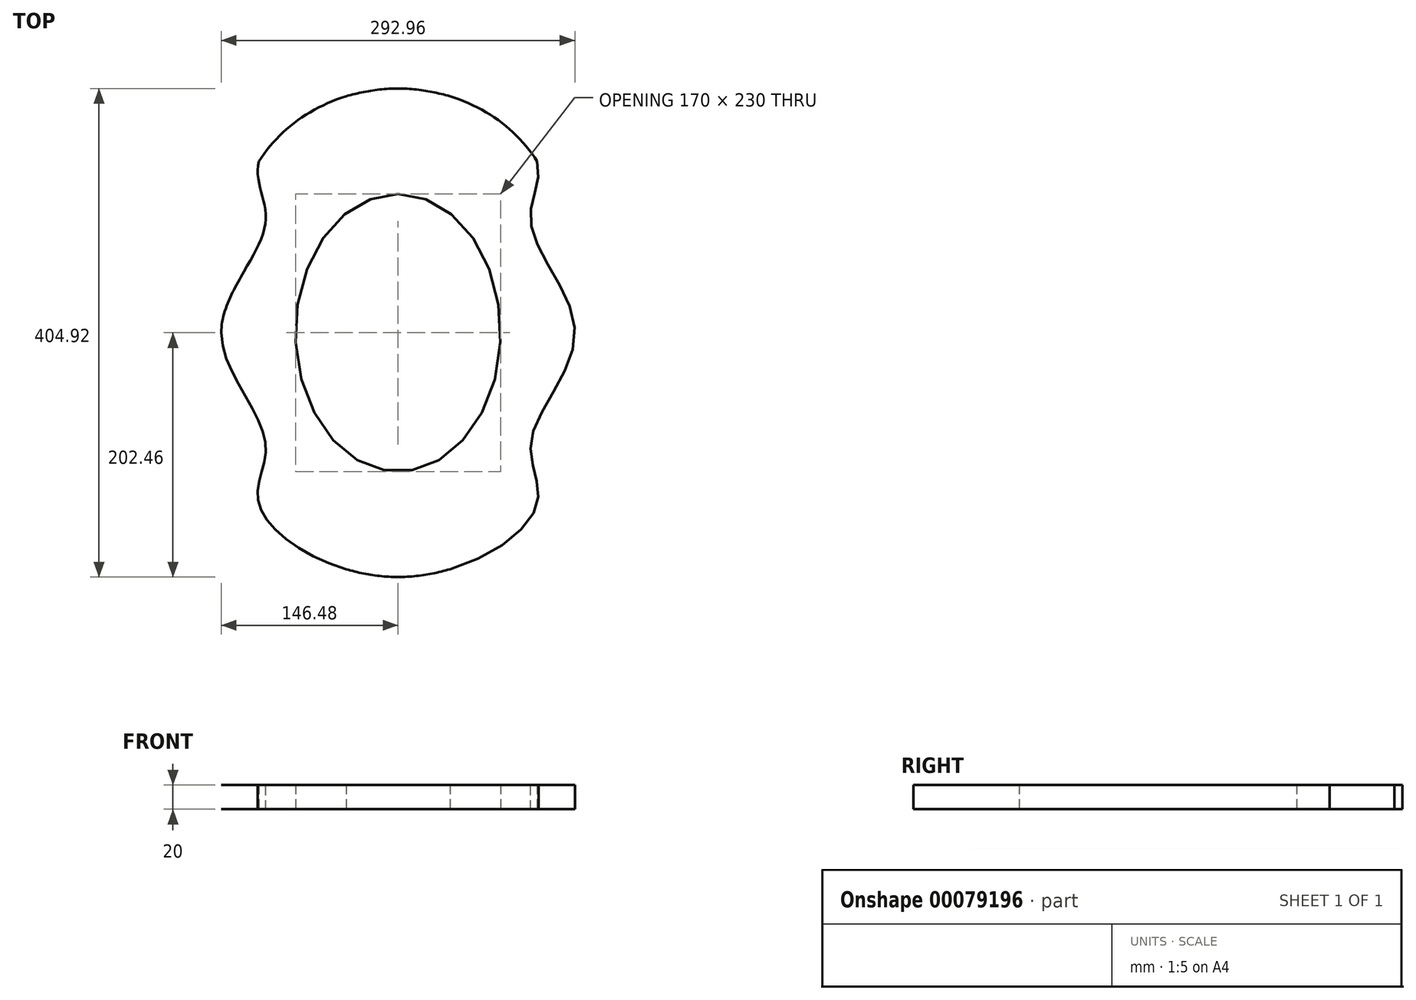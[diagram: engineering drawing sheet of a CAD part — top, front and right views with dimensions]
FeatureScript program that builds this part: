
annotation { "Feature Type Name" : "Feature", "Feature Type Description" : "" }
export const myFeature = defineFeature(function(context is Context, id is Id, definition is map)
    precondition{}
    {
        {
            var Q0;
            Q0=qCreatedBy(makeId("Top.planeOp"),FACE);
            var sketch = newSketch(context, id + "F0", { "sketchPlane" : qUnion([Q0])});
            skPoint(sketch, "E0", {"position": v(150.32, -165.76) * mm});
            skPoint(sketch, "E1", {"position": v(107.37, -221.56) * mm});
            skPoint(sketch, "E2", {"position": v(69.02, -211.72) * mm});
            skPoint(sketch, "E3", {"position": v(0, -246.18) * mm});
            skPoint(sketch, "E4", {"position": v(138.05, -177.25) * mm});
            skPoint(sketch, "E5", {"position": v(146.48, 0) * mm});
            skPoint(sketch, "E6", {"position": v(132.68, -82.88) * mm});
            skLineSegment(sketch, "E7", {"start": v(0, 292) * mm, "end": v(0, -246.18) * mm, "construction": true});
            skPoint(sketch, "E8.MirrorP", {"position": v(-146.48, 0) * mm});
            skPoint(sketch, "E9.MirrorP", {"position": v(-132.68, -82.88) * mm});
            skPoint(sketch, "E10.MirrorP", {"position": v(-150.32, -165.76) * mm});
            skPoint(sketch, "E11.MirrorP", {"position": v(-138.05, -177.25) * mm});
            skPoint(sketch, "E12.MirrorP", {"position": v(-107.37, -221.56) * mm});
            skPoint(sketch, "E13.MirrorP", {"position": v(-69.02, -211.72) * mm});
            skPoint(sketch, "E14", {"position": v(0, 0) * mm});
            skPoint(sketch, "E15", {"position": v(-146.25, -161.4) * mm});
            skPoint(sketch, "E16", {"position": v(-136.87, -189.28) * mm});
            skPoint(sketch, "E17", {"position": v(-146.26, -172.33) * mm});
            skPoint(sketch, "E18", {"position": v(-131.04, -210.06) * mm});
            skPoint(sketch, "E19", {"position": v(-94.82, -218.38) * mm});
            skPoint(sketch, "E20", {"position": v(-60.59, -222.84) * mm});
            skPoint(sketch, "E21", {"position": v(-67.25, -214.49) * mm});
            skPoint(sketch, "E22", {"position": v(-72.48, -210.2) * mm});
            skPoint(sketch, "E23", {"position": v(-119.37, -219.05) * mm});
            skPoint(sketch, "E24", {"position": v(-149.89, -167.68) * mm});
            skPoint(sketch, "E25.MirrorP", {"position": v(60.59, -222.84) * mm});
            skPoint(sketch, "E26.MirrorP", {"position": v(67.25, -214.49) * mm});
            skPoint(sketch, "E27.MirrorP", {"position": v(72.48, -210.2) * mm});
            skPoint(sketch, "E28.MirrorP", {"position": v(94.82, -218.38) * mm});
            skPoint(sketch, "E29.MirrorP", {"position": v(119.37, -219.05) * mm});
            skPoint(sketch, "E30.MirrorP", {"position": v(136.87, -189.28) * mm});
            skPoint(sketch, "E31.MirrorP", {"position": v(146.26, -172.33) * mm});
            skPoint(sketch, "E32.MirrorP", {"position": v(149.89, -167.68) * mm});
            skPoint(sketch, "E33.MirrorP", {"position": v(146.25, -161.4) * mm});
            skPoint(sketch, "E34", {"position": v(-139.73, -175.31) * mm});
            skPoint(sketch, "E35.MirrorP", {"position": v(131.04, -210.06) * mm});
            skPoint(sketch, "E36.MirrorP", {"position": v(-132.68, 82.88) * mm});
            skPoint(sketch, "E37.MirrorP", {"position": v(-139.73, 175.31) * mm});
            skPoint(sketch, "E38.MirrorP", {"position": v(-150.32, 165.76) * mm});
            skPoint(sketch, "E39.MirrorP", {"position": v(69.02, 211.72) * mm});
            skPoint(sketch, "E40.MirrorP", {"position": v(150.32, 165.76) * mm});
            skPoint(sketch, "E41.MirrorP", {"position": v(-67.25, 214.49) * mm});
            skPoint(sketch, "E42.MirrorP", {"position": v(131.04, 210.06) * mm});
            skPoint(sketch, "E43.MirrorP", {"position": v(60.59, 222.84) * mm});
            skPoint(sketch, "E44.MirrorP", {"position": v(119.37, 219.05) * mm});
            skPoint(sketch, "E45.MirrorP", {"position": v(136.87, 189.28) * mm});
            skPoint(sketch, "E46.MirrorP", {"position": v(-72.48, 210.2) * mm});
            skPoint(sketch, "E47.MirrorP", {"position": v(-138.05, 177.25) * mm});
            skPoint(sketch, "E48.MirrorP", {"position": v(-69.02, 211.72) * mm});
            skPoint(sketch, "E49.MirrorP", {"position": v(72.48, 210.2) * mm});
            skPoint(sketch, "E50.MirrorP", {"position": v(-146.25, 161.4) * mm});
            skPoint(sketch, "E51.MirrorP", {"position": v(-136.87, 189.28) * mm});
            skPoint(sketch, "E52.MirrorP", {"position": v(138.05, 177.25) * mm});
            skPoint(sketch, "E53.MirrorP", {"position": v(67.25, 214.49) * mm});
            skPoint(sketch, "E54.MirrorP", {"position": v(-149.89, 167.68) * mm});
            skPoint(sketch, "E55.MirrorP", {"position": v(149.89, 167.68) * mm});
            skPoint(sketch, "E56.MirrorP", {"position": v(-107.37, 221.56) * mm});
            skPoint(sketch, "E57.MirrorP", {"position": v(-94.82, 218.38) * mm});
            skPoint(sketch, "E58.MirrorP", {"position": v(146.26, 172.33) * mm});
            skPoint(sketch, "E59.MirrorP", {"position": v(107.37, 221.56) * mm});
            skPoint(sketch, "E60.MirrorP", {"position": v(-131.04, 210.06) * mm});
            skPoint(sketch, "E61.MirrorP", {"position": v(94.82, 218.38) * mm});
            skPoint(sketch, "E62.MirrorP", {"position": v(146.25, 161.4) * mm});
            skPoint(sketch, "E63.MirrorP", {"position": v(0, 246.18) * mm});
            skPoint(sketch, "E64.MirrorP", {"position": v(-146.26, 172.33) * mm});
            skPoint(sketch, "E65.MirrorP", {"position": v(-119.37, 219.05) * mm});
            skPoint(sketch, "E66.MirrorP", {"position": v(-60.59, 222.84) * mm});
            skPoint(sketch, "E67.MirrorP", {"position": v(132.68, 82.88) * mm});
            skFitSpline(sketch, "E68", {"points": [v(-146.48, 0) * mm, v(-132.68, 82.88) * mm, v(-146.25, 161.4) * mm, v(-150.32, 165.76) * mm, v(-149.89, 167.68) * mm, v(-146.26, 172.33) * mm, v(-139.73, 175.31) * mm, v(-138.05, 177.25) * mm, v(-136.87, 189.28) * mm, v(-131.04, 210.06) * mm, v(-119.37, 219.05) * mm, v(-107.37, 221.56) * mm, v(-94.82, 218.38) * mm, v(-72.48, 210.2) * mm, v(-69.02, 211.72) * mm, v(-67.25, 214.49) * mm, v(-60.59, 222.84) * mm, v(0, 246.18) * mm, v(60.59, 222.84) * mm, v(67.25, 214.49) * mm, v(69.02, 211.72) * mm, v(72.48, 210.2) * mm, v(94.82, 218.38) * mm, v(107.37, 221.56) * mm, v(119.37, 219.05) * mm, v(131.04, 210.06) * mm, v(136.87, 189.28) * mm, v(138.05, 177.25) * mm, v(146.26, 172.33) * mm, v(149.89, 167.68) * mm, v(150.32, 165.76) * mm, v(146.25, 161.4) * mm, v(132.68, 82.88) * mm, v(146.48, 0) * mm, v(132.68, -82.88) * mm, v(146.25, -161.4) * mm, v(150.32, -165.76) * mm, v(149.89, -167.68) * mm, v(146.26, -172.33) * mm, v(138.05, -177.25) * mm, v(136.87, -189.28) * mm, v(131.04, -210.06) * mm, v(119.37, -219.05) * mm, v(107.37, -221.56) * mm, v(94.82, -218.38) * mm, v(72.48, -210.2) * mm, v(69.02, -211.72) * mm, v(67.25, -214.49) * mm, v(60.59, -222.84) * mm, v(0, -246.18) * mm, v(-60.59, -222.84) * mm, v(-67.25, -214.49) * mm, v(-69.02, -211.72) * mm, v(-72.48, -210.2) * mm, v(-94.82, -218.38) * mm, v(-107.37, -221.56) * mm, v(-119.37, -219.05) * mm, v(-131.04, -210.06) * mm, v(-136.87, -189.28) * mm, v(-138.05, -177.25) * mm, v(-139.73, -175.31) * mm, v(-146.26, -172.33) * mm, v(-149.89, -167.68) * mm, v(-150.32, -165.76) * mm, v(-146.25, -161.4) * mm, v(-132.68, -82.88) * mm, v(-146.48, 0) * mm]});
            skPoint(sketch, "E69", {"position": v(0, 295) * mm});
            skPoint(sketch, "E70", {"position": v(-30, 295) * mm});
            skPoint(sketch, "E71", {"position": v(-225, 0) * mm});
            skPoint(sketch, "E72", {"position": v(-225, 100) * mm});
            skPoint(sketch, "E73.MirrorP", {"position": v(225, 100) * mm});
            skPoint(sketch, "E74.MirrorP", {"position": v(225, -60) * mm});
            skLineSegment(sketch, "E75", {"start": v(0, 0) * mm, "end": v(-373.3, 215.53) * mm, "construction": true});
            skLineSegment(sketch, "E76", {"start": v(0, 0) * mm, "end": v(-204.64, 354.44) * mm, "construction": true});
            skLineSegment(sketch, "E77", {"start": v(-225, 0) * mm, "end": v(-225, 100) * mm});
            skLineSegment(sketch, "E78", {"start": v(-30, 295) * mm, "end": v(0, 295) * mm});
            skPoint(sketch, "E79", {"position": v(-30, 100) * mm});
            skArc(sketch, "E80", {"start": v(-30, 295) * mm, "mid": v(-167.89, 237.89) * mm, "end": v(-225, 100) * mm});
            skLineSegment(sketch, "E81.MirrorCS", {"start": v(225, 0) * mm, "end": v(225, 100) * mm});
            skArc(sketch, "E82.MirrorCS", {"start": v(30, 295) * mm, "mid": v(167.89, 237.89) * mm, "end": v(225, 100) * mm});
            skLineSegment(sketch, "E83.MirrorCS", {"start": v(30, 295) * mm, "end": v(0, 295) * mm});
            skArc(sketch, "E84.MirrorCS", {"start": v(-30, -295) * mm, "mid": v(-167.89, -237.89) * mm, "end": v(-225, -100) * mm});
            skLineSegment(sketch, "E85.MirrorCS", {"start": v(-225, 0) * mm, "end": v(-225, -100) * mm});
            skLineSegment(sketch, "E86.MirrorCS", {"start": v(225, 0) * mm, "end": v(225, -100) * mm});
            skArc(sketch, "E87.MirrorCS", {"start": v(30, -295) * mm, "mid": v(167.89, -237.89) * mm, "end": v(225, -100) * mm});
            skLineSegment(sketch, "E88.MirrorCS", {"start": v(30, -295) * mm, "end": v(0, -295) * mm});
            skLineSegment(sketch, "E89.MirrorCS", {"start": v(-30, -295) * mm, "end": v(0, -295) * mm});
            skEllipse(sketch, "E90", {"center": v(0, 82.88) * mm, "majorRadius": 132.68 * mm, "minorRadius": 119.58 * mm, "majorAxis": v(1, 0)});
            skSolve(sketch);
        }
        {
            var Q0;
            {var subQ0=sQuery(id+"F0.wireOp",EDGE,"E90");var subQ1=sQuery(id+"F0.wireOp",EDGE,"E68");var subQ2=makeQuery(id+"F0.imprint","INTERSECT",VERTEX,{"disambiguationData":[OD(0.0)],"derivedFrom":[subQ1,subQ0]});Q0=makeQuery(id+"F0.imprint","IMPRINT",FACE,{"disambiguationData":[TD([[makeQuery(id+"F0.imprint","IMPRINT",EDGE,{"disambiguationData":[TD([[subQ2,1.0]])],"derivedFrom":subQ1}),-1.0]])]});}
            var sketch = newSketch(context, id + "F1", { "sketchPlane" : qUnion([Q0])});
            skFitSpline(sketch, "E91.0", {"points": [v(-146.48, 0) * mm, v(-146.48, 25.45) * mm, v(-122.55, 75.68) * mm, v(-141.58, 161.6) * mm, v(-150.97, 165.24) * mm, v(-149.84, 167.93) * mm, v(-146.88, 173.13) * mm, v(-139.54, 174.98) * mm, v(-137.39, 177.3) * mm, v(-137.38, 190.15) * mm, v(-133.28, 211.38) * mm, v(-119.9, 219.69) * mm, v(-106.83, 222.51) * mm, v(-95.46, 219.19) * mm, v(-72.9, 208.32) * mm, v(-68.89, 211.56) * mm, v(-66.98, 214.97) * mm, v(-60.9, 225.94) * mm, v(0, 260.58) * mm, v(60.9, 225.94) * mm, v(66.98, 214.97) * mm, v(68.89, 211.56) * mm, v(72.9, 208.32) * mm, v(95.47, 219.19) * mm, v(106.82, 222.52) * mm, v(119.95, 219.67) * mm, v(133.09, 211.44) * mm, v(138.2, 189.9) * mm, v(135.3, 175.97) * mm, v(146.9, 173.38) * mm, v(149.81, 167.94) * mm, v(150.98, 165.24) * mm, v(141.57, 161.6) * mm, v(122.55, 75.68) * mm, v(158.6, 0) * mm, v(122.55, -75.68) * mm, v(141.57, -161.6) * mm, v(150.98, -165.24) * mm, v(149.81, -167.94) * mm, v(146.9, -173.38) * mm, v(135.3, -175.97) * mm, v(138.2, -189.9) * mm, v(133.09, -211.44) * mm, v(119.95, -219.67) * mm, v(106.82, -222.52) * mm, v(95.47, -219.19) * mm, v(72.9, -208.32) * mm, v(68.89, -211.56) * mm, v(66.98, -214.97) * mm, v(60.9, -225.94) * mm, v(0, -260.58) * mm, v(-60.9, -225.94) * mm, v(-66.98, -214.97) * mm, v(-68.89, -211.56) * mm, v(-72.9, -208.32) * mm, v(-95.46, -219.19) * mm, v(-106.83, -222.51) * mm, v(-119.9, -219.69) * mm, v(-133.28, -211.38) * mm, v(-137.38, -190.15) * mm, v(-137.39, -177.3) * mm, v(-139.54, -174.98) * mm, v(-146.88, -173.13) * mm, v(-149.84, -167.93) * mm, v(-150.97, -165.24) * mm, v(-141.58, -161.6) * mm, v(-122.55, -75.68) * mm, v(-146.48, -25.45) * mm, v(-146.48, 0) * mm]});
            skEllipticalArc(sketch, "E92.0", {});
            skEllipticalArc(sketch, "E93.MirrorC", {});
            skFitSpline(sketch, "E94.trimOffspring", {"points": [v(-146.48, 0) * mm, v(-146.48, 25.45) * mm, v(-122.55, 75.68) * mm, v(-141.58, 161.6) * mm, v(-150.97, 165.24) * mm, v(-149.84, 167.93) * mm, v(-146.88, 173.13) * mm, v(-139.54, 174.98) * mm, v(-137.39, 177.3) * mm, v(-137.38, 190.15) * mm, v(-133.28, 211.38) * mm, v(-119.9, 219.69) * mm, v(-106.83, 222.51) * mm, v(-95.46, 219.19) * mm, v(-72.9, 208.32) * mm, v(-68.89, 211.56) * mm, v(-66.98, 214.97) * mm, v(-60.9, 225.94) * mm, v(0, 260.58) * mm, v(60.9, 225.94) * mm, v(66.98, 214.97) * mm, v(68.89, 211.56) * mm, v(72.9, 208.32) * mm, v(95.47, 219.19) * mm, v(106.82, 222.52) * mm, v(119.95, 219.67) * mm, v(133.09, 211.44) * mm, v(138.2, 189.9) * mm, v(135.3, 175.97) * mm, v(146.9, 173.38) * mm, v(149.81, 167.94) * mm, v(150.98, 165.24) * mm, v(141.57, 161.6) * mm, v(122.55, 75.68) * mm, v(158.6, 0) * mm, v(122.55, -75.68) * mm, v(141.57, -161.6) * mm, v(150.98, -165.24) * mm, v(149.81, -167.94) * mm, v(146.9, -173.38) * mm, v(135.3, -175.97) * mm, v(138.2, -189.9) * mm, v(133.09, -211.44) * mm, v(119.95, -219.67) * mm, v(106.82, -222.52) * mm, v(95.47, -219.19) * mm, v(72.9, -208.32) * mm, v(68.89, -211.56) * mm, v(66.98, -214.97) * mm, v(60.9, -225.94) * mm, v(0, -260.58) * mm, v(-60.9, -225.94) * mm, v(-66.98, -214.97) * mm, v(-68.89, -211.56) * mm, v(-72.9, -208.32) * mm, v(-95.46, -219.19) * mm, v(-106.83, -222.51) * mm, v(-119.9, -219.69) * mm, v(-133.28, -211.38) * mm, v(-137.38, -190.15) * mm, v(-137.39, -177.3) * mm, v(-139.54, -174.98) * mm, v(-146.88, -173.13) * mm, v(-149.84, -167.93) * mm, v(-150.97, -165.24) * mm, v(-141.58, -161.6) * mm, v(-122.55, -75.68) * mm, v(-146.48, -25.45) * mm, v(-146.48, 0) * mm]});
            skPoint(sketch, "E95", {"position": v(0, 202.46) * mm});
            skPoint(sketch, "E96", {"position": v(-110, 90) * mm});
            skPoint(sketch, "E97", {"position": v(-115, 143) * mm});
            skPoint(sketch, "E98.MirrorP", {"position": v(115, 143) * mm});
            skPoint(sketch, "E99.MirrorP", {"position": v(110, 90) * mm});
            skPoint(sketch, "E100.MirrorP", {"position": v(-110, -90) * mm});
            skPoint(sketch, "E101.MirrorP", {"position": v(-115, -143) * mm});
            skPoint(sketch, "E102.MirrorP", {"position": v(0, -202.46) * mm});
            skPoint(sketch, "E103.MirrorP", {"position": v(115, -143) * mm});
            skPoint(sketch, "E104.MirrorP", {"position": v(110, -90) * mm});
            skFitSpline(sketch, "E105", {"points": [v(-146.48, 0) * mm, v(-110, 90) * mm, v(-115, 143) * mm, v(0, 202.46) * mm, v(115, 143) * mm, v(110, 90) * mm, v(146.48, 0) * mm, v(110, -90) * mm, v(115, -143) * mm, v(0, -202.46) * mm, v(-115, -143) * mm, v(-110, -90) * mm, v(-146.48, 0) * mm]});
            skFitSpline(sketch, "E106.trimOffspring", {"points": [v(-146.48, 0) * mm, v(-146.48, 25.45) * mm, v(-122.55, 75.68) * mm, v(-141.58, 161.6) * mm, v(-150.97, 165.24) * mm, v(-149.84, 167.93) * mm, v(-146.88, 173.13) * mm, v(-139.54, 174.98) * mm, v(-137.39, 177.3) * mm, v(-137.38, 190.15) * mm, v(-133.28, 211.38) * mm, v(-119.9, 219.69) * mm, v(-106.83, 222.51) * mm, v(-95.46, 219.19) * mm, v(-72.9, 208.32) * mm, v(-68.89, 211.56) * mm, v(-66.98, 214.97) * mm, v(-60.9, 225.94) * mm, v(0, 260.58) * mm, v(60.9, 225.94) * mm, v(66.98, 214.97) * mm, v(68.89, 211.56) * mm, v(72.9, 208.32) * mm, v(95.47, 219.19) * mm, v(106.82, 222.52) * mm, v(119.95, 219.67) * mm, v(133.09, 211.44) * mm, v(138.2, 189.9) * mm, v(135.3, 175.97) * mm, v(146.9, 173.38) * mm, v(149.81, 167.94) * mm, v(150.98, 165.24) * mm, v(141.57, 161.6) * mm, v(122.55, 75.68) * mm, v(158.6, 0) * mm, v(122.55, -75.68) * mm, v(141.57, -161.6) * mm, v(150.98, -165.24) * mm, v(149.81, -167.94) * mm, v(146.9, -173.38) * mm, v(135.3, -175.97) * mm, v(138.2, -189.9) * mm, v(133.09, -211.44) * mm, v(119.95, -219.67) * mm, v(106.82, -222.52) * mm, v(95.47, -219.19) * mm, v(72.9, -208.32) * mm, v(68.89, -211.56) * mm, v(66.98, -214.97) * mm, v(60.9, -225.94) * mm, v(0, -260.58) * mm, v(-60.9, -225.94) * mm, v(-66.98, -214.97) * mm, v(-68.89, -211.56) * mm, v(-72.9, -208.32) * mm, v(-95.46, -219.19) * mm, v(-106.83, -222.51) * mm, v(-119.9, -219.69) * mm, v(-133.28, -211.38) * mm, v(-137.38, -190.15) * mm, v(-137.39, -177.3) * mm, v(-139.54, -174.98) * mm, v(-146.88, -173.13) * mm, v(-149.84, -167.93) * mm, v(-150.97, -165.24) * mm, v(-141.58, -161.6) * mm, v(-122.55, -75.68) * mm, v(-146.48, -25.45) * mm, v(-146.48, 0) * mm]});
            skFitSpline(sketch, "E107.trimOffspring", {"points": [v(-146.48, 0) * mm, v(-146.48, 25.45) * mm, v(-122.55, 75.68) * mm, v(-141.58, 161.6) * mm, v(-150.97, 165.24) * mm, v(-149.84, 167.93) * mm, v(-146.88, 173.13) * mm, v(-139.54, 174.98) * mm, v(-137.39, 177.3) * mm, v(-137.38, 190.15) * mm, v(-133.28, 211.38) * mm, v(-119.9, 219.69) * mm, v(-106.83, 222.51) * mm, v(-95.46, 219.19) * mm, v(-72.9, 208.32) * mm, v(-68.89, 211.56) * mm, v(-66.98, 214.97) * mm, v(-60.9, 225.94) * mm, v(0, 260.58) * mm, v(60.9, 225.94) * mm, v(66.98, 214.97) * mm, v(68.89, 211.56) * mm, v(72.9, 208.32) * mm, v(95.47, 219.19) * mm, v(106.82, 222.52) * mm, v(119.95, 219.67) * mm, v(133.09, 211.44) * mm, v(138.2, 189.9) * mm, v(135.3, 175.97) * mm, v(146.9, 173.38) * mm, v(149.81, 167.94) * mm, v(150.98, 165.24) * mm, v(141.57, 161.6) * mm, v(122.55, 75.68) * mm, v(158.6, 0) * mm, v(122.55, -75.68) * mm, v(141.57, -161.6) * mm, v(150.98, -165.24) * mm, v(149.81, -167.94) * mm, v(146.9, -173.38) * mm, v(135.3, -175.97) * mm, v(138.2, -189.9) * mm, v(133.09, -211.44) * mm, v(119.95, -219.67) * mm, v(106.82, -222.52) * mm, v(95.47, -219.19) * mm, v(72.9, -208.32) * mm, v(68.89, -211.56) * mm, v(66.98, -214.97) * mm, v(60.9, -225.94) * mm, v(0, -260.58) * mm, v(-60.9, -225.94) * mm, v(-66.98, -214.97) * mm, v(-68.89, -211.56) * mm, v(-72.9, -208.32) * mm, v(-95.46, -219.19) * mm, v(-106.83, -222.51) * mm, v(-119.9, -219.69) * mm, v(-133.28, -211.38) * mm, v(-137.38, -190.15) * mm, v(-137.39, -177.3) * mm, v(-139.54, -174.98) * mm, v(-146.88, -173.13) * mm, v(-149.84, -167.93) * mm, v(-150.97, -165.24) * mm, v(-141.58, -161.6) * mm, v(-122.55, -75.68) * mm, v(-146.48, -25.45) * mm, v(-146.48, 0) * mm]});
            skFitSpline(sketch, "E108.trimOffspring", {"points": [v(-146.48, 0) * mm, v(-146.48, 25.45) * mm, v(-122.55, 75.68) * mm, v(-141.58, 161.6) * mm, v(-150.97, 165.24) * mm, v(-149.84, 167.93) * mm, v(-146.88, 173.13) * mm, v(-139.54, 174.98) * mm, v(-137.39, 177.3) * mm, v(-137.38, 190.15) * mm, v(-133.28, 211.38) * mm, v(-119.9, 219.69) * mm, v(-106.83, 222.51) * mm, v(-95.46, 219.19) * mm, v(-72.9, 208.32) * mm, v(-68.89, 211.56) * mm, v(-66.98, 214.97) * mm, v(-60.9, 225.94) * mm, v(0, 260.58) * mm, v(60.9, 225.94) * mm, v(66.98, 214.97) * mm, v(68.89, 211.56) * mm, v(72.9, 208.32) * mm, v(95.47, 219.19) * mm, v(106.82, 222.52) * mm, v(119.95, 219.67) * mm, v(133.09, 211.44) * mm, v(138.2, 189.9) * mm, v(135.3, 175.97) * mm, v(146.9, 173.38) * mm, v(149.81, 167.94) * mm, v(150.98, 165.24) * mm, v(141.57, 161.6) * mm, v(122.55, 75.68) * mm, v(158.6, 0) * mm, v(122.55, -75.68) * mm, v(141.57, -161.6) * mm, v(150.98, -165.24) * mm, v(149.81, -167.94) * mm, v(146.9, -173.38) * mm, v(135.3, -175.97) * mm, v(138.2, -189.9) * mm, v(133.09, -211.44) * mm, v(119.95, -219.67) * mm, v(106.82, -222.52) * mm, v(95.47, -219.19) * mm, v(72.9, -208.32) * mm, v(68.89, -211.56) * mm, v(66.98, -214.97) * mm, v(60.9, -225.94) * mm, v(0, -260.58) * mm, v(-60.9, -225.94) * mm, v(-66.98, -214.97) * mm, v(-68.89, -211.56) * mm, v(-72.9, -208.32) * mm, v(-95.46, -219.19) * mm, v(-106.83, -222.51) * mm, v(-119.9, -219.69) * mm, v(-133.28, -211.38) * mm, v(-137.38, -190.15) * mm, v(-137.39, -177.3) * mm, v(-139.54, -174.98) * mm, v(-146.88, -173.13) * mm, v(-149.84, -167.93) * mm, v(-150.97, -165.24) * mm, v(-141.58, -161.6) * mm, v(-122.55, -75.68) * mm, v(-146.48, -25.45) * mm, v(-146.48, 0) * mm]});
            skEllipticalArc(sketch, "E109.trimOffspring", {});
            skEllipticalArc(sketch, "E110.trimOffspring", {});
            skEllipticalArc(sketch, "E111.trimOffspring", {});
            skEllipticalArc(sketch, "E112.trimOffspring", {});
            skFitSpline(sketch, "E113.trimOffspring", {"points": [v(-146.48, 0) * mm, v(-146.48, 25.45) * mm, v(-122.55, 75.68) * mm, v(-141.58, 161.6) * mm, v(-150.97, 165.24) * mm, v(-149.84, 167.93) * mm, v(-146.88, 173.13) * mm, v(-139.54, 174.98) * mm, v(-137.39, 177.3) * mm, v(-137.38, 190.15) * mm, v(-133.28, 211.38) * mm, v(-119.9, 219.69) * mm, v(-106.83, 222.51) * mm, v(-95.46, 219.19) * mm, v(-72.9, 208.32) * mm, v(-68.89, 211.56) * mm, v(-66.98, 214.97) * mm, v(-60.9, 225.94) * mm, v(0, 260.58) * mm, v(60.9, 225.94) * mm, v(66.98, 214.97) * mm, v(68.89, 211.56) * mm, v(72.9, 208.32) * mm, v(95.47, 219.19) * mm, v(106.82, 222.52) * mm, v(119.95, 219.67) * mm, v(133.09, 211.44) * mm, v(138.2, 189.9) * mm, v(135.3, 175.97) * mm, v(146.9, 173.38) * mm, v(149.81, 167.94) * mm, v(150.98, 165.24) * mm, v(141.57, 161.6) * mm, v(122.55, 75.68) * mm, v(158.6, 0) * mm, v(122.55, -75.68) * mm, v(141.57, -161.6) * mm, v(150.98, -165.24) * mm, v(149.81, -167.94) * mm, v(146.9, -173.38) * mm, v(135.3, -175.97) * mm, v(138.2, -189.9) * mm, v(133.09, -211.44) * mm, v(119.95, -219.67) * mm, v(106.82, -222.52) * mm, v(95.47, -219.19) * mm, v(72.9, -208.32) * mm, v(68.89, -211.56) * mm, v(66.98, -214.97) * mm, v(60.9, -225.94) * mm, v(0, -260.58) * mm, v(-60.9, -225.94) * mm, v(-66.98, -214.97) * mm, v(-68.89, -211.56) * mm, v(-72.9, -208.32) * mm, v(-95.46, -219.19) * mm, v(-106.83, -222.51) * mm, v(-119.9, -219.69) * mm, v(-133.28, -211.38) * mm, v(-137.38, -190.15) * mm, v(-137.39, -177.3) * mm, v(-139.54, -174.98) * mm, v(-146.88, -173.13) * mm, v(-149.84, -167.93) * mm, v(-150.97, -165.24) * mm, v(-141.58, -161.6) * mm, v(-122.55, -75.68) * mm, v(-146.48, -25.45) * mm, v(-146.48, 0) * mm]});
            skEllipse(sketch, "E114", {"center": v(0, 0) * mm, "majorRadius": 115 * mm, "minorRadius": 85 * mm, "majorAxis": v(0, 1)});
            const initialGuessF1  = {"E92.0": [0, 0.08288104439999998, 1, 0, 0.13267715999999996, 0.11958350000000001, 0, 0.055173648266843435], "E93.MirrorC": [0, -0.08288104439999998, 1, 0, 0.13267715999999996, 0.11958350000000001, 3.141592653589793, 3.1966594490639286], "E109.trimOffspring": [0, -0.08288104439999998, 1, 0, 0.13267715999999996, 0.11958350000000001, 4.382070923725125, 5.042707037044202], "E110.trimOffspring": [0, 0.08288104439999998, 1, 0, 0.13267715999999996, 0.11958350000000001, 1.2404782701353567, 1.9011143834544768], "E111.trimOffspring": [0, 0.08288104439999998, 1, 0, 0.13267715999999996, 0.11958350000000001, 3.0865258581156554, 3.141592653589793], "E112.trimOffspring": [0, -0.08288104439999998, 1, 0, 0.13267715999999996, 0.11958350000000001, 6.228011658912739, 0]};
            skSetInitialGuess(sketch, initialGuessF1);
            skSolve(sketch);
        }
        {
            var Q0;
            {var subQ0=sQuery(id+"F1.wireOp",EDGE,"E109.trimOffspring");var subQ1=sQuery(id+"F1.wireOp",EDGE,"E105");var subQ8=makeQuery(id+"F1.imprint","INTERSECT",VERTEX,{"disambiguationData":[OD(1.0)],"derivedFrom":[subQ1,subQ0]});Q0=makeQuery(id+"F1.imprint","IMPRINT",FACE,{"disambiguationData":[TD([[makeQuery(id+"F1.imprint","IMPRINT",EDGE,{"disambiguationData":[TD([[subQ8,-1.0]])],"derivedFrom":subQ1}),-1.0]])]});}
            var Q1;
            {var subQ0=sQuery(id+"F1.wireOp",EDGE,"E110.trimOffspring");var subQ1=sQuery(id+"F1.wireOp",EDGE,"E105");var subQ6=makeQuery(id+"F1.imprint","INTERSECT",VERTEX,{"derivedFrom":[subQ1,subQ0]});Q1=makeQuery(id+"F1.imprint","IMPRINT",FACE,{"disambiguationData":[TD([[makeQuery(id+"F1.imprint","IMPRINT",EDGE,{"disambiguationData":[TD([[subQ6,1.0]])],"derivedFrom":subQ1}),-1.0]])]});}
            extrude(context, id + "F2", {"entities" : qUnion([Q0, Q1]), "depth" : 20 * mm, "offsetDistance" : 25 * mm});
        }
    });
